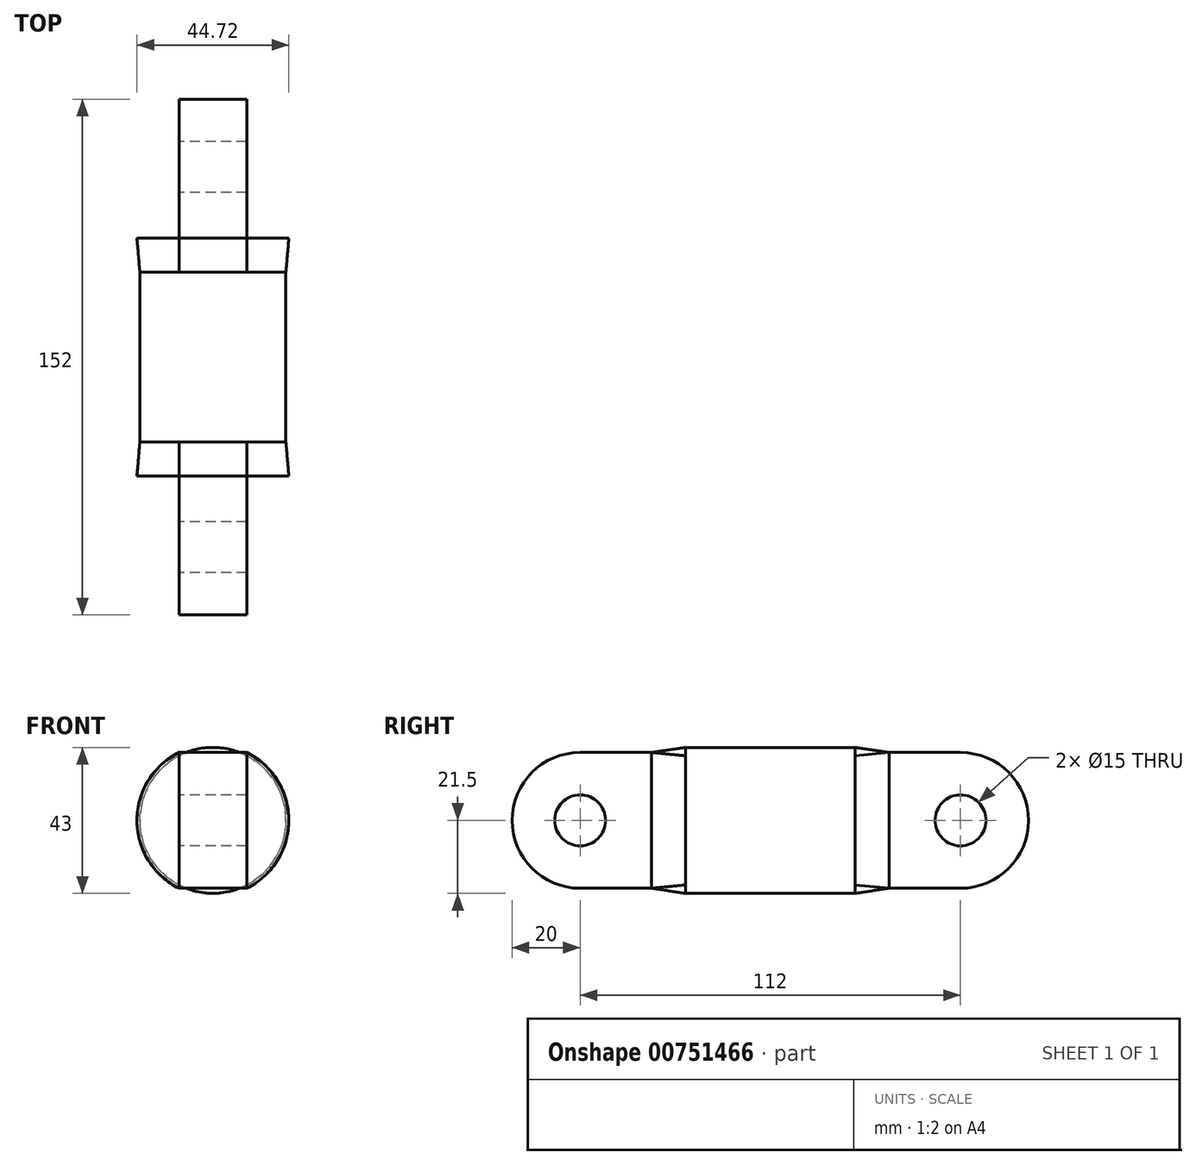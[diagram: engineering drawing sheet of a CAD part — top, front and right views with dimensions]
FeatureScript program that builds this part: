
annotation { "Feature Type Name" : "Feature", "Feature Type Description" : "" }
export const myFeature = defineFeature(function(context is Context, id is Id, definition is map)
    precondition{}
    {
        {
            var Q0;
            Q0=qCreatedBy(makeId("Right.planeOp"),FACE);
            var sketch = newSketch(context, id + "F0", { "sketchPlane" : qUnion([Q0])});
            skArc(sketch, "E0", {"start": v(0, -20) * mm, "mid": v(20, 0) * mm, "end": v(0, 20) * mm});
            skCircle(sketch, "E1", {"center": v(0, 0) * mm, "radius": 7.5 * mm});
            skLineSegment(sketch, "E2", {"start": v(0, 0) * mm, "end": v(-73, 0) * mm, "construction": true});
            skLineSegment(sketch, "E3", {"start": v(0, 20) * mm, "end": v(-21, 20) * mm});
            skLineSegment(sketch, "E4", {"start": v(0, -20) * mm, "end": v(-21, -20) * mm});
            skLineSegment(sketch, "E5", {"start": v(-73, -20) * mm, "end": v(-73, 20) * mm});
            skArc(sketch, "E6", {"start": v(-97.68, 24.03) * mm, "mid": v(-137, 0) * mm, "end": v(-97.68, -24.03) * mm});
            skCircle(sketch, "E7", {"center": v(0, 0) * mm, "radius": 20 * mm, "construction": true});
            skCircle(sketch, "E8", {"center": v(-110, 0) * mm, "radius": 10 * mm});
            skLineSegment(sketch, "E9", {"start": v(-21, 20) * mm, "end": v(-21, -20) * mm});
            skArc(sketch, "E10", {"start": v(-97.68, -24.03) * mm, "mid": v(-83, 0) * mm, "end": v(-97.68, 24.03) * mm, "construction": true});
            skLineSegment(sketch, "E11", {"start": v(-81, 20) * mm, "end": v(-81, -20) * mm, "construction": true});
            skLineSegment(sketch, "E12", {"start": v(-73, 20) * mm, "end": v(-81, 20) * mm});
            skLineSegment(sketch, "E13", {"start": v(-73, -20) * mm, "end": v(-81, -20) * mm});
            skArc(sketch, "E14", {"start": v(-97.68, 24.03) * mm, "mid": v(-89.58, 21.02) * mm, "end": v(-81, 20) * mm});
            skArc(sketch, "E15", {"start": v(-81, -20) * mm, "mid": v(-89.58, -21.02) * mm, "end": v(-97.68, -24.03) * mm});
            skSolve(sketch);
        }
        {
            var Q0;
            Q0=makeQuery(id+"F0.imprint","IMPRINT",FACE,{"disambiguationData":[TD([[makeQuery(id+"F0.imprint","IMPRINT",EDGE,{"derivedFrom":sQuery(id+"F0.wireOp",EDGE,"E0")}),1.0]])]});
            extrude(context, id + "F1", {"entities" : qUnion([Q0]), "endBound" : BoundingType.SYMMETRIC, "depth" : 20 * mm, "offsetDistance" : 25 * mm});
        }
        {
            var Q0;
            Q0=makeQuery(id+"F1.opExtrude","SWEPT_FACE",FACE,{"disambiguationData":[OSD([sQuery(id+"F0.wireOp",EDGE,"E9")])]});
            var sketch = newSketch(context, id + "F2", { "sketchPlane" : qUnion([Q0])});
            skCircle(sketch, "E16", {"center": v(0, 0) * mm, "radius": 21.5 * mm, "construction": true});
            skArc(sketch, "E17", {"start": v(-10, 20) * mm, "mid": v(-22.36, 0) * mm, "end": v(-10, -20) * mm});
            skLineSegment(sketch, "E18", {"start": v(-10, 20) * mm, "end": v(10, 20) * mm});
            skLineSegment(sketch, "E19", {"start": v(-10, -20) * mm, "end": v(10, -20) * mm});
            skLineSegment(sketch, "E20", {"start": v(0, 20) * mm, "end": v(0, -20) * mm, "construction": true});
            skArc(sketch, "E21.MirrorCS", {"start": v(10, 20) * mm, "mid": v(22.36, 0) * mm, "end": v(10, -20) * mm});
            skSolve(sketch);
        }
        {
            var Q0;
            Q0=makeQuery(id+"F2.imprint","IMPRINT",FACE,{"disambiguationData":[TD([[makeQuery(id+"F2.imprint","IMPRINT",EDGE,{"derivedFrom":sQuery(id+"F2.wireOp",EDGE,"E18")}),1.0]])]});
            cPlane(context, id + "F3", {"entities" : qUnion([Q0]), "cplaneType" : CPlaneType.OFFSET, "offset" : 10 * mm, "width" : 150 * mm, "height" : 150 * mm});
        }
        {
            var Q0;
            Q0=qCreatedBy(id+"F3.planeOp",FACE);
            var sketch = newSketch(context, id + "F4", { "sketchPlane" : qUnion([Q0])});
            skArc(sketch, "E22.0", {"start": v(-10, 19.03) * mm, "mid": v(-21.5, 0) * mm, "end": v(-10, -19.03) * mm});
            skLineSegment(sketch, "E23", {"start": v(-10, 19.03) * mm, "end": v(-10, -19.03) * mm});
            skLineSegment(sketch, "E24", {"start": v(10, 19.03) * mm, "end": v(10, -19.03) * mm});
            skArc(sketch, "E25.trimOffspring", {"start": v(10, -19.03) * mm, "mid": v(21.5, 0) * mm, "end": v(10, 19.03) * mm});
            skArc(sketch, "E26", {"start": v(10, 19.03) * mm, "mid": v(0, 21.5) * mm, "end": v(-10, 19.03) * mm});
            skArc(sketch, "E27", {"start": v(-10, -19.03) * mm, "mid": v(0, -21.5) * mm, "end": v(10, -19.03) * mm});
            skSolve(sketch);
        }
        {
            var Q1;
            Q1=qSketchRegion(id+"F2",true);
            var Q2;
            Q2=qSketchRegion(id+"F4",true);
            loft(context, id + "F5", {"operationType" : NewBodyOperationType.ADD, "sheetProfilesArray" : [{ "sheetProfileEntities" : qUnion([Q1]) }, { "sheetProfileEntities" : qUnion([Q2]) }]});
        }
        {
            var Q0;
            {var subQ0=makeQuery(id+"F4.imprint","IMPRINT",EDGE,{"derivedFrom":sQuery(id+"F4.wireOp",EDGE,"E23")});var subQ1=makeQuery(id+"F4.imprint","IMPRINT",EDGE,{"derivedFrom":sQuery(id+"F4.wireOp",EDGE,"E24")});Q0=makeQuery(id+"F5.opLoft","CAP_FACE",FACE,{"disambiguationData":[OSD([makeQuery(id+"F4.imprint","IMPRINT",FACE,{"disambiguationData":[TD([[makeQuery(id+"F4.imprint","IMPRINT",EDGE,{"derivedFrom":sQuery(id+"F4.wireOp",EDGE,"E22.0")}),1.0]])]}),makeQuery(id+"F4.imprint","IMPRINT",FACE,{"disambiguationData":[TD([[subQ1,1.0]])]}),makeQuery(id+"F4.imprint","IMPRINT",FACE,{"disambiguationData":[TD([[subQ0,1.0]])]})])],"isStart":true});}
            var Q1;
            Q1=makeQuery(id+"Flma1KrjLcidEWh_1.opExtrude","SWEPT_FACE",FACE,{"disambiguationData":[OSD([sQuery(id+"F0.wireOp",EDGE,"E5")])]});
            extrude(context, id + "F6", {"entities" : qUnion([Q0]), "operationType" : NewBodyOperationType.ADD, "depth" : 25 * mm, "endBoundEntityFace" : qUnion([Q1]), "offsetDistance" : 25 * mm});
        }
        {
            var Q0;
            Q0=makeQuery(id+"F1.opExtrude","SWEPT_BODY",BODY,{"disambiguationData":[OSD([sQuery(id+"F0.wireOp",EDGE,"E0"),sQuery(id+"F0.wireOp",EDGE,"E1"),sQuery(id+"F0.wireOp",EDGE,"E3"),sQuery(id+"F0.wireOp",EDGE,"E4"),sQuery(id+"F0.wireOp",EDGE,"E9")])]});
            var Q1;
            {var subQ0=makeQuery(id+"F4.imprint","IMPRINT",EDGE,{"derivedFrom":sQuery(id+"F4.wireOp",EDGE,"E23")});var subQ1=makeQuery(id+"F4.imprint","IMPRINT",EDGE,{"derivedFrom":sQuery(id+"F4.wireOp",EDGE,"E24")});Q1=makeQuery(id+"F6.opExtrude","CAP_FACE",FACE,{"disambiguationData":[OSD([makeQuery(id+"F4.imprint","IMPRINT",FACE,{"disambiguationData":[TD([[makeQuery(id+"F4.imprint","IMPRINT",EDGE,{"derivedFrom":sQuery(id+"F4.wireOp",EDGE,"E22.0")}),1.0]])]}),makeQuery(id+"F4.imprint","IMPRINT",FACE,{"disambiguationData":[TD([[subQ1,1.0]])]}),makeQuery(id+"F4.imprint","IMPRINT",FACE,{"disambiguationData":[TD([[subQ0,1.0]])]})])],"isStart":false});}
            mirror(context, id + "F7", {"operationType" : NewBodyOperationType.ADD, "entities" : qUnion([Q0]), "mirrorPlane" : qUnion([Q1])});
        }
    });
